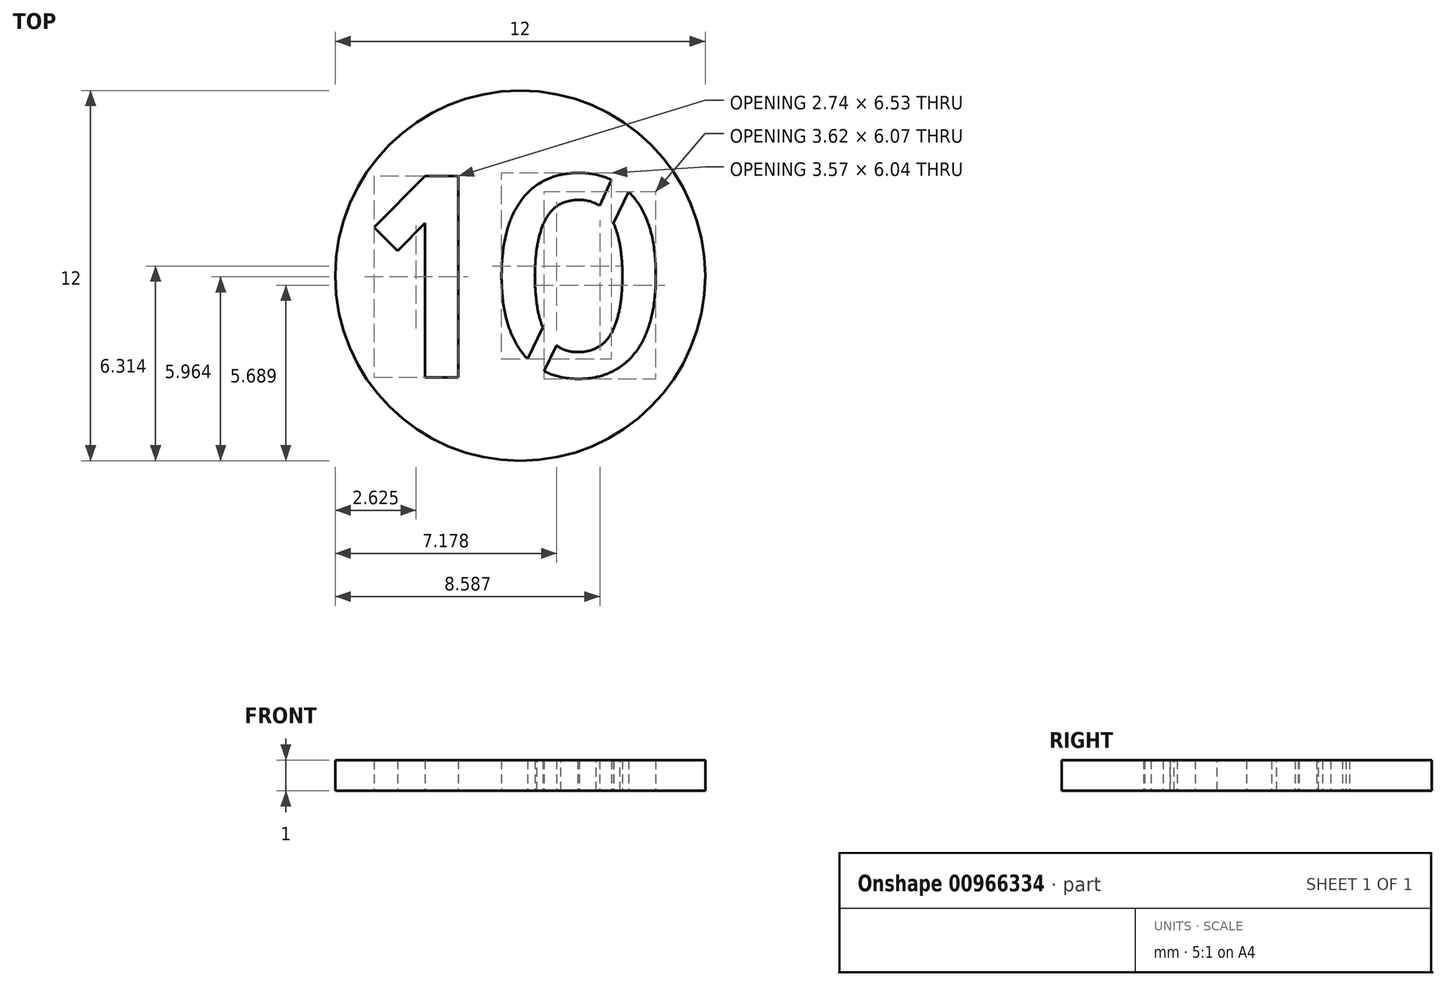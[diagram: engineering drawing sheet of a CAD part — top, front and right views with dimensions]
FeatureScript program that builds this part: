
annotation { "Feature Type Name" : "Feature", "Feature Type Description" : "" }
export const myFeature = defineFeature(function(context is Context, id is Id, definition is map)
    precondition{}
    {
        {
            var Q0;
            Q0=qCreatedBy(makeId("Top.planeOp"),FACE);
            var sketch = newSketch(context, id + "F0", { "sketchPlane" : qUnion([Q0])});
            skCircle(sketch, "E0", {"center": v(0, 0) * mm, "radius": 6 * mm});
            skSolve(sketch);
        }
        {
            var Q0;
            Q0=makeQuery(id+"F0.imprint","IMPRINT",FACE,{"disambiguationData":[TD([[makeQuery(id+"F0.imprint","IMPRINT",EDGE,{"derivedFrom":sQuery(id+"F0.wireOp",EDGE,"E0")}),1.0]])]});
            var sketch = newSketch(context, id + "F1", { "sketchPlane" : qUnion([Q0])});
            skText(sketch, "E1", { "text": "10", "fontName": "AllertaStencil-Regular.ttf"});
            const initialGuessF1  = {"E1": [-0.005, -0.0033, 1, 0, 0.00653]};
            skSetInitialGuess(sketch, initialGuessF1);
            skSolve(sketch);
        }
        {
            var Q0;
            Q0=makeQuery(id+"F0.imprint","IMPRINT",FACE,{"disambiguationData":[TD([[makeQuery(id+"F0.imprint","IMPRINT",EDGE,{"derivedFrom":sQuery(id+"F0.wireOp",EDGE,"E0")}),1.0]])]});
            extrude(context, id + "F2", {"entities" : qUnion([Q0]), "depth" : 1 * mm, "offsetDistance" : 25.4 * mm});
        }
        {
            var Q0;
            Q0 = qSketchRegion(id + "F1", true);
            extrude(context, id + "F3", {"entities" : qUnion([Q0]), "operationType" : NewBodyOperationType.REMOVE, "depth" : 1.4 * mm, "offsetDistance" : 25.4 * mm});
        }
    });
